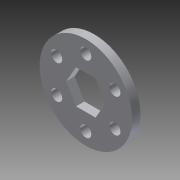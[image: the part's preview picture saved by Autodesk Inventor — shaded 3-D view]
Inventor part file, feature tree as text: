
AUTODESK INVENTOR PART (.ipt)
format: ipt  version: 2014 (Build 180170000, 170)  size: 102,400 bytes
history: native  units: in
note: dims shown in document units (in); Inventor stores cm internally (conversion verified against a paired STEP export)
features: extrude x1, sketch x1
ambient origin geometry x8: Origin, YZ Plane, XZ Plane, XY Plane, X Axis, Y Axis, Z Axis, Center Point
bodies: Solid1 (feature_tree)
feature tree (2):
  extrude  "Extrusion1"  Depth=0.504in
  sketch  "Sketch1"  dims[d0=1.375in d1=0.504in d2=0.164in d3=0.5in d4=2.3622in d6=360.0deg d8=0.125in d9=0.0in]
